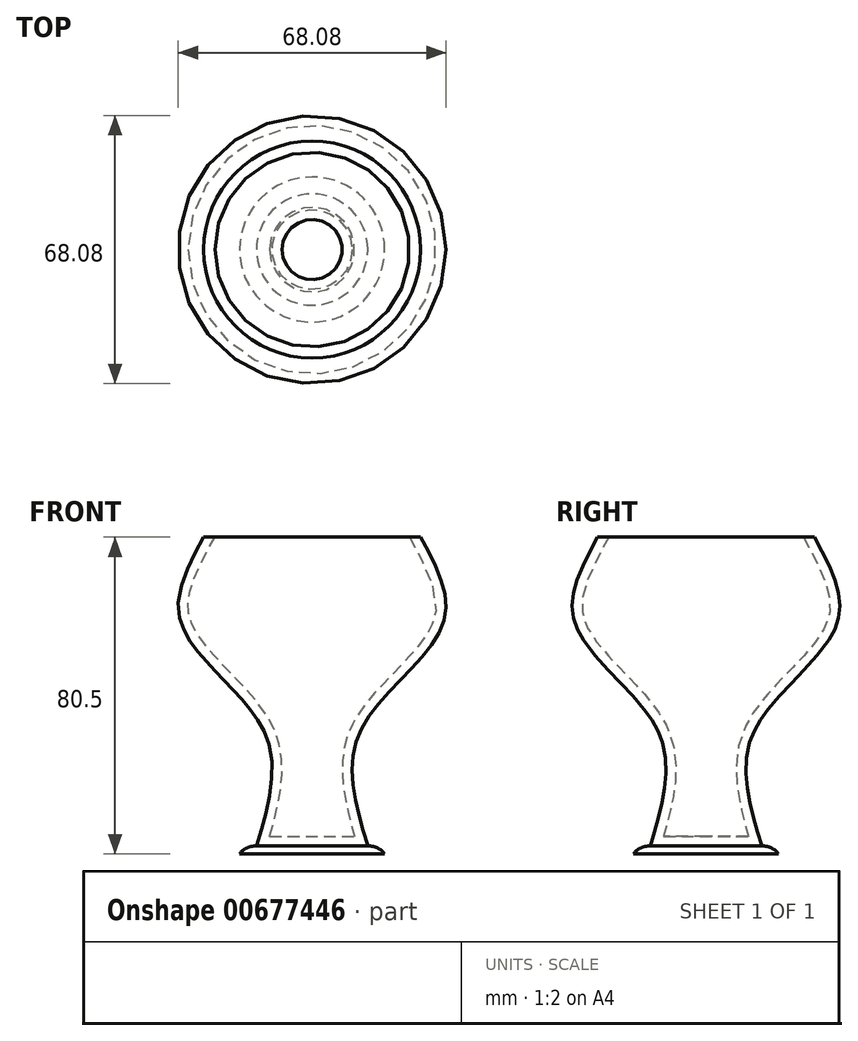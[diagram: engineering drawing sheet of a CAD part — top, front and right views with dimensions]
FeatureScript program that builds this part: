
annotation { "Feature Type Name" : "Feature", "Feature Type Description" : "" }
export const myFeature = defineFeature(function(context is Context, id is Id, definition is map)
    precondition{}
    {
        {
            var Q0;
            Q0=qCreatedBy(makeId("Top.planeOp"),FACE);
            var sketch = newSketch(context, id + "F0", { "sketchPlane" : qUnion([Q0])});
            skCircle(sketch, "E0", {"center": v(0, 0) * mm, "radius": 14.14 * mm});
            skSolve(sketch);
        }
        {
            var Q0;
            Q0=qCreatedBy(makeId("Top.planeOp"),FACE);
            cPlane(context, id + "F1", {"entities" : qUnion([Q0]), "cplaneType" : CPlaneType.OFFSET, "offset" : 78.5 * mm, "width" : 150 * mm, "height" : 150 * mm});
        }
        {
            var Q0;
            Q0=qCreatedBy(id+"F1.planeOp",FACE);
            var sketch = newSketch(context, id + "F2", { "sketchPlane" : qUnion([Q0])});
            skCircle(sketch, "E1", {"center": v(0, 0) * mm, "radius": 27.56 * mm});
            skSolve(sketch);
        }
        {
            var Q0;
            Q0=qCreatedBy(makeId("Top.planeOp"),FACE);
            cPlane(context, id + "F3", {"entities" : qUnion([Q0]), "cplaneType" : CPlaneType.OFFSET, "offset" : 28 * mm, "width" : 150 * mm, "height" : 150 * mm});
        }
        {
            var Q0;
            Q0=qCreatedBy(makeId("Top.planeOp"),FACE);
            cPlane(context, id + "F4", {"entities" : qUnion([Q0]), "cplaneType" : CPlaneType.OFFSET, "offset" : 59.7 * mm, "width" : 150 * mm, "height" : 150 * mm});
        }
        {
            var Q0;
            Q0=qCreatedBy(id+"F4.planeOp",FACE);
            var sketch = newSketch(context, id + "F5", { "sketchPlane" : qUnion([Q0])});
            skCircle(sketch, "E2", {"center": v(0, 0) * mm, "radius": 33.97 * mm});
            skSolve(sketch);
        }
        {
            var Q0;
            Q0=qCreatedBy(id+"F3.planeOp",FACE);
            var sketch = newSketch(context, id + "F6", { "sketchPlane" : qUnion([Q0])});
            skCircle(sketch, "E3", {"center": v(0, 0) * mm, "radius": 11.66 * mm});
            skSolve(sketch);
        }
        {
            var Q0;
            Q0=makeQuery(id+"F0.imprint","IMPRINT",FACE,{"disambiguationData":[TD([[makeQuery(id+"F0.imprint","IMPRINT",EDGE,{"derivedFrom":sQuery(id+"F0.wireOp",EDGE,"E0")}),1.0]])]});
            var Q1;
            Q1=makeQuery(id+"F6.imprint","IMPRINT",FACE,{"disambiguationData":[TD([[makeQuery(id+"F6.imprint","IMPRINT",EDGE,{"derivedFrom":sQuery(id+"F6.wireOp",EDGE,"E3")}),1.0]])]});
            var Q2;
            Q2=makeQuery(id+"F5.imprint","IMPRINT",FACE,{"disambiguationData":[TD([[makeQuery(id+"F5.imprint","IMPRINT",EDGE,{"derivedFrom":sQuery(id+"F5.wireOp",EDGE,"E2")}),1.0]])]});
            var Q3;
            Q3=makeQuery(id+"F2.imprint","IMPRINT",FACE,{"disambiguationData":[TD([[makeQuery(id+"F2.imprint","IMPRINT",EDGE,{"derivedFrom":sQuery(id+"F2.wireOp",EDGE,"E1")}),1.0]])]});
            loft(context, id + "F7", {"sheetProfilesArray" : [{ "sheetProfileEntities" : qUnion([Q0]) }, { "sheetProfileEntities" : qUnion([Q1]) }, { "sheetProfileEntities" : qUnion([Q2]) }, { "sheetProfileEntities" : qUnion([Q3]) }]});
        }
        {
            var Q0;
            Q0=makeQuery(id+"F7.opLoft","CAP_FACE",FACE,{"disambiguationData":[OSD([makeQuery(id+"F2.imprint","IMPRINT",FACE,{"disambiguationData":[TD([[makeQuery(id+"F2.imprint","IMPRINT",EDGE,{"derivedFrom":sQuery(id+"F2.wireOp",EDGE,"E1")}),1.0]])]})])],"isStart":true});
            shell(context, id + "F8", {"entities" : qUnion([Q0]), "thickness" : 2.5 * mm});
        }
        {
            var Q0;
            Q0=makeQuery(id+"F7.opLoft","CAP_FACE",FACE,{"disambiguationData":[OSD([makeQuery(id+"F0.imprint","IMPRINT",FACE,{"disambiguationData":[TD([[makeQuery(id+"F0.imprint","IMPRINT",EDGE,{"derivedFrom":sQuery(id+"F0.wireOp",EDGE,"E0")}),1.0]])]})])],"isStart":true});
            var sketch = newSketch(context, id + "F9", { "sketchPlane" : qUnion([Q0])});
            skCircle(sketch, "E4", {"center": v(0, 0) * mm, "radius": 18.43 * mm});
            skSolve(sketch);
        }
        {
            var Q0;
            Q0 = qSketchRegion(id + "F9", true);
            extrude(context, id + "F10", {"entities" : qUnion([Q0]), "operationType" : NewBodyOperationType.ADD, "depth" : 2 * mm, "offsetDistance" : 25 * mm});
        }
        {
            var Q0;
            Q0=makeQuery(id+"F10.opExtrude","CAP_EDGE",EDGE,{"disambiguationData":[OSD([sQuery(id+"F9.wireOp",EDGE,"E4")])],"isStart":true});
            fillet(context, id + "F11", {"entities" : qUnion([Q0]), "radius" : 5 * mm, "tangentPropagation" : true, "allowEdgeOverflow" : false});
        }
    });
